# Revit family: Cabinet-Teknion-CETT_Two_High_Tall_Cabinet_Door-R2023
name_source: partatom
category: Furniture
units: mm (PartAtom-declared; Revit-internal decimal feet)

## family parameters
Always vertical = Yes
Cut with Voids When Loaded = No
Enable Cutting in Views = No
OmniClass Number = 23.40.20.00
OmniClass Title = General Furniture and Specialties
Render Appearance Source = Family Geometry
Room Calculation Point = No
Shared = Yes
Work Plane-Based = No

## types (6) — shared parameters
Assembly Code = E2020200
Manufacturer = Teknion
Manufacturer Fax = 416.661.4586
Part Number = CETT
Product Documentation Link = https://www.teknion.com
Product Line = Storage Cabinets
Product Page URL = https://www.teknion.com
Series = Expansion Casework+
Sustainability Data = https://www.teknion.com
URL = www.teknion.com
Unit Weight URL = http://www.teknion.com
Warranty = http://www.teknion.com
zero-valued in all types: Default Elevation

## per-type parameters (varying)
| type | Actual Depth | Description | Height | Model | Shelf |
| 29D,84H | 30.024 " | Two-High Tall Cabinet – Door(s),29D,84H | 84 " | CETT29_84 | No |
| 29D,90H | 30.024 " | Two-High Tall Cabinet – Door(s),29D,90H | 90 " | CETT29_90 | Yes |
| 29D,96H | 30.024 " | Two-High Tall Cabinet – Door(s),29D,96H | 96 " | CETT29_96 | Yes |
| 24D,84H | 25.024 " | Two-High Tall Cabinet – Door(s),24D,84H | 84 " | CETT24_84 | No |
| 24D,90H | 25.024 " | Two-High Tall Cabinet – Door(s),24D,90H | 90 " | CETT24_90 | Yes |
| 24D,96H | 25.024 " | Two-High Tall Cabinet – Door(s),24D,96H | 96 " | CETT24_96 | Yes |

## geometry (parser evidence)
native form markers: Sweep x2
no freeform markers — native parametric forms only
